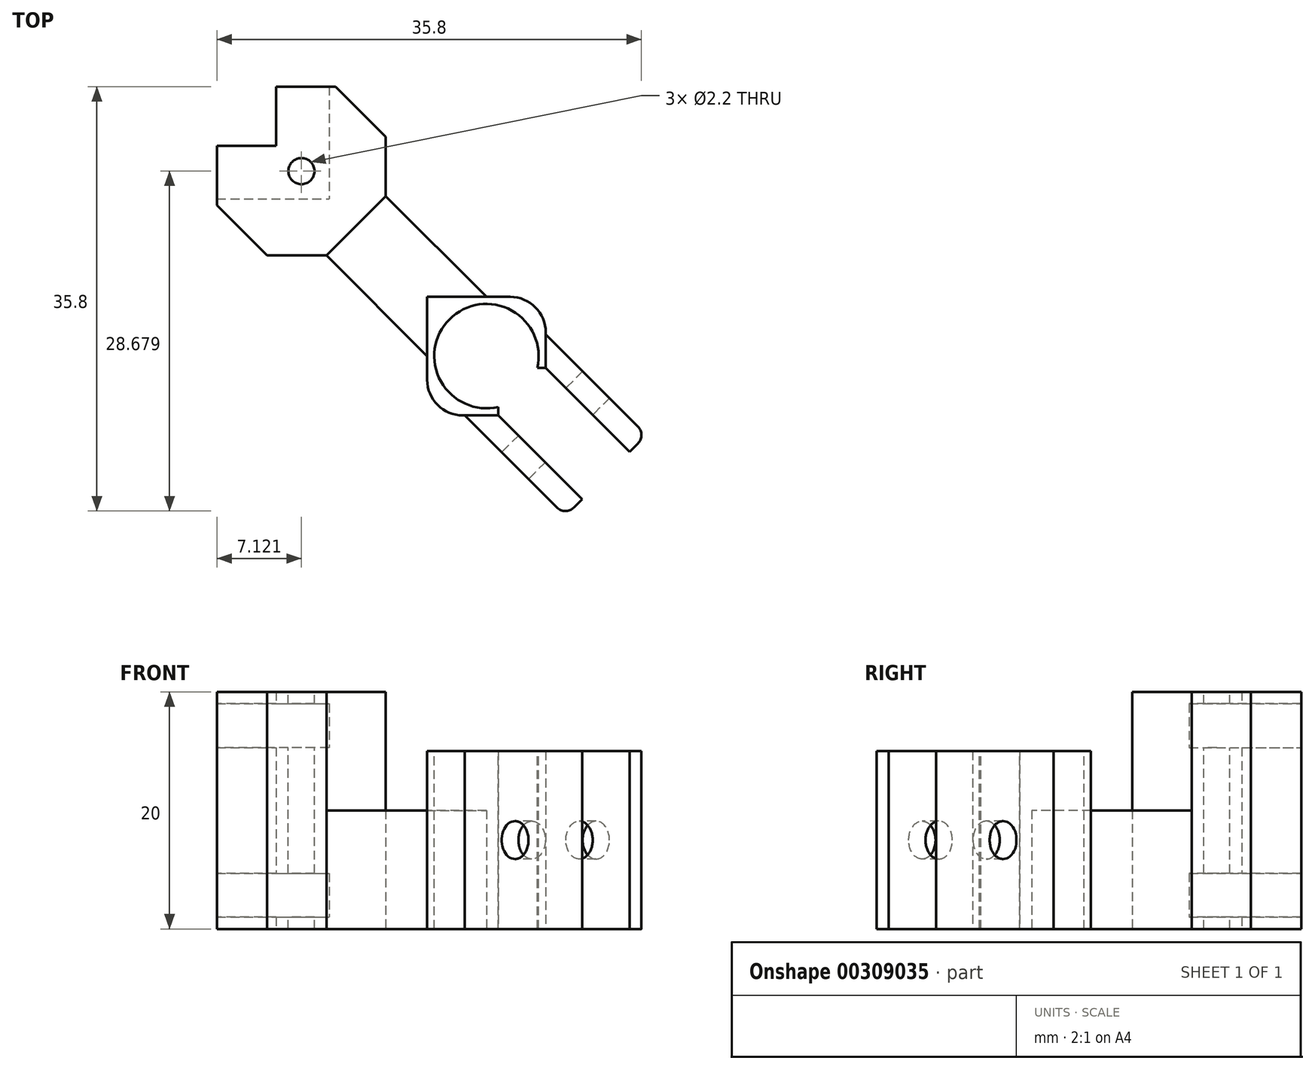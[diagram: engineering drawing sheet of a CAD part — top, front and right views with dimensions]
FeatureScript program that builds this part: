
annotation { "Feature Type Name" : "Feature", "Feature Type Description" : "" }
export const myFeature = defineFeature(function(context is Context, id is Id, definition is map)
    precondition{}
    {
        {
            var Q0;
            Q0=qCreatedBy(makeId("Top.planeOp"),FACE);
            var sketch = newSketch(context, id + "F0", { "sketchPlane" : qUnion([Q0])});
            skLineSegment(sketch, "E0", {"start": v(0, 0) * mm, "end": v(-5, 0) * mm});
            skLineSegment(sketch, "E1", {"start": v(-5, 0) * mm, "end": v(-5, 5) * mm});
            skLineSegment(sketch, "E2", {"start": v(-5, 5) * mm, "end": v(0, 5) * mm});
            skLineSegment(sketch, "E3", {"start": v(0, 5) * mm, "end": v(0, 10) * mm});
            skLineSegment(sketch, "E4", {"start": v(0, 10) * mm, "end": v(5, 10) * mm});
            skLineSegment(sketch, "E5", {"start": v(5, 10) * mm, "end": v(5, 5) * mm});
            skLineSegment(sketch, "E6", {"start": v(-5, 0) * mm, "end": v(-0.76, -4.24) * mm});
            skLineSegment(sketch, "E7", {"start": v(5, 10) * mm, "end": v(9.24, 5.76) * mm});
            skLineSegment(sketch, "E8", {"start": v(9.24, 5.76) * mm, "end": v(9.24, 0.76) * mm});
            skLineSegment(sketch, "E9", {"start": v(-0.76, -4.24) * mm, "end": v(4.24, -4.24) * mm});
            skLineSegment(sketch, "E10", {"start": v(9.24, 0.76) * mm, "end": v(17.73, -7.73) * mm});
            skLineSegment(sketch, "E11", {"start": v(4.24, -4.24) * mm, "end": v(12.73, -12.73) * mm});
            skLineSegment(sketch, "E12", {"start": v(12.73, -12.73) * mm, "end": v(12.73, -17.73) * mm});
            skLineSegment(sketch, "E13", {"start": v(12.73, -17.73) * mm, "end": v(22.73, -17.73) * mm});
            skLineSegment(sketch, "E14", {"start": v(22.73, -17.73) * mm, "end": v(22.73, -7.73) * mm});
            skLineSegment(sketch, "E15", {"start": v(22.73, -7.73) * mm, "end": v(17.73, -7.73) * mm});
            skLineSegment(sketch, "E16", {"start": v(4.24, -4.24) * mm, "end": v(9.24, 0.76) * mm});
            skPoint(sketch, "E17", {"position": v(22.73, -13.73) * mm});
            skPoint(sketch, "E18", {"position": v(18.73, -17.73) * mm});
            skLineSegment(sketch, "E19", {"start": v(22.73, -13.73) * mm, "end": v(29.8, -20.8) * mm});
            skLineSegment(sketch, "E20", {"start": v(18.73, -17.73) * mm, "end": v(25.8, -24.8) * mm});
            skLineSegment(sketch, "E21", {"start": v(29.8, -20.8) * mm, "end": v(31.21, -19.38) * mm});
            skLineSegment(sketch, "E22", {"start": v(31.21, -19.38) * mm, "end": v(22.73, -10.9) * mm});
            skLineSegment(sketch, "E23", {"start": v(25.8, -24.8) * mm, "end": v(24.38, -26.21) * mm});
            skLineSegment(sketch, "E24", {"start": v(24.38, -26.21) * mm, "end": v(15.9, -17.73) * mm});
            skSolve(sketch);
        }
        {
            var Q0;
            Q0=makeQuery(id+"F0.imprint","IMPRINT",FACE,{"disambiguationData":[TD([[makeQuery(id+"F0.imprint","IMPRINT",EDGE,{"derivedFrom":sQuery(id+"F0.wireOp",EDGE,"E1")}),-1.0]])]});
            extrude(context, id + "F1", {"entities" : qUnion([Q0]), "depth" : 20 * mm});
        }
        {
            var Q0;
            Q0=makeQuery(id+"F0.imprint","IMPRINT",FACE,{"disambiguationData":[TD([[makeQuery(id+"F0.imprint","IMPRINT",EDGE,{"derivedFrom":sQuery(id+"F0.wireOp",EDGE,"E10")}),-1.0]])]});
            extrude(context, id + "F2", {"entities" : qUnion([Q0]), "operationType" : NewBodyOperationType.ADD, "depth" : 10 * mm});
        }
        {
            var Q0;
            Q0=makeQuery(id+"F1.opExtrude","SWEPT_FACE",FACE,{"disambiguationData":[OSD([sQuery(id+"F0.wireOp",EDGE,"E4")])]});
            var sketch = newSketch(context, id + "F3", { "sketchPlane" : qUnion([Q0])});
            skPoint(sketch, "E25", {"position": v(0, 19) * mm});
            skPoint(sketch, "E26", {"position": v(0, 15.6) * mm});
            skPoint(sketch, "E27", {"position": v(0, 1) * mm});
            skPoint(sketch, "E28", {"position": v(0, 4.4) * mm});
            skLineSegment(sketch, "E29", {"start": v(0, 19) * mm, "end": v(-5, 19) * mm});
            skLineSegment(sketch, "E30", {"start": v(-5, 19) * mm, "end": v(-5, 15.6) * mm});
            skLineSegment(sketch, "E31", {"start": v(-5, 15.6) * mm, "end": v(0, 15.6) * mm});
            skSolve(sketch);
        }
        {
            var Q0;
            Q0=qSketchRegion(id+"F3",true);
            var Q1;
            {var subQ0=sQuery(id+"F3.wireOp",EDGE,"E29");Q1=makeQuery(id+"F3.imprint","IMPRINT",FACE,{"disambiguationData":[TD([[makeQuery(id+"F3.imprint","IMPRINT",EDGE,{"derivedFrom":subQ0}),1.0]])]});}
            extrude(context, id + "F4", {"entities" : qUnion([Q0, Q1]), "operationType" : NewBodyOperationType.REMOVE, "oppositeDirection" : true, "depth" : 25 * mm});
        }
        {
            var Q0;
            Q0=makeQuery(id+"F1.opExtrude","SWEPT_FACE",FACE,{"disambiguationData":[OSD([sQuery(id+"F0.wireOp",EDGE,"E2")])]});
            var sketch = newSketch(context, id + "F5", { "sketchPlane" : qUnion([Q0])});
            skLineSegment(sketch, "E32", {"start": v(0, 19) * mm, "end": v(5, 19) * mm});
            skLineSegment(sketch, "E33", {"start": v(5, 19) * mm, "end": v(5, 15.6) * mm});
            skLineSegment(sketch, "E34", {"start": v(5, 15.6) * mm, "end": v(0, 15.6) * mm});
            skLineSegment(sketch, "E35", {"start": v(0, 15.6) * mm, "end": v(0, 19) * mm});
            skSolve(sketch);
        }
        {
            var Q0;
            Q0=makeQuery(id+"F5.imprint","IMPRINT",FACE,{"disambiguationData":[TD([[makeQuery(id+"F5.imprint","IMPRINT",EDGE,{"derivedFrom":sQuery(id+"F5.wireOp",EDGE,"E32")}),-1.0]])]});
            extrude(context, id + "F6", {"entities" : qUnion([Q0]), "operationType" : NewBodyOperationType.REMOVE, "oppositeDirection" : true, "depth" : 25 * mm});
        }
        {
            var Q0;
            Q0=makeQuery(id+"F1.opExtrude","SWEPT_FACE",FACE,{"disambiguationData":[OSD([sQuery(id+"F0.wireOp",EDGE,"E7")])]});
            var sketch = newSketch(context, id + "F7", { "sketchPlane" : qUnion([Q0])});
            skLineSegment(sketch, "E36", {"start": v(3.54, 15.6) * mm, "end": v(-2.46, 15.6) * mm});
            skLineSegment(sketch, "E37", {"start": v(-2.46, 15.6) * mm, "end": v(-2.46, 19) * mm});
            skLineSegment(sketch, "E38", {"start": v(-2.46, 19) * mm, "end": v(3.54, 19) * mm});
            skLineSegment(sketch, "E39", {"start": v(3.54, 19) * mm, "end": v(3.54, 15.6) * mm});
            skSolve(sketch);
        }
        {
            var Q0;
            Q0=qSketchRegion(id+"F7",true);
            extrude(context, id + "F8", {"entities" : qUnion([Q0]), "operationType" : NewBodyOperationType.REMOVE, "oppositeDirection" : true, "depth" : 25 * mm});
        }
        {
            var Q0;
            {var subQ3=sQuery(id+"F0.wireOp",EDGE,"E4");Q0=makeQuery(id+"F4.boolean.opBoolean","SPLIT",FACE,{"disambiguationData":[TD([makeQuery(id+"F4.opExtrude","SWEPT_FACE",FACE,{"disambiguationData":[OSD([sQuery(id+"F3.wireOp",EDGE,"E31")])]})])],"derivedFrom":makeQuery(id+"F1.opExtrude","SWEPT_FACE",FACE,{"disambiguationData":[OSD([subQ3])]})});}
            var sketch = newSketch(context, id + "F9", { "sketchPlane" : qUnion([Q0])});
            skPoint(sketch, "E40", {"position": v(0, 1) * mm});
            skPoint(sketch, "E41", {"position": v(0, 4.4) * mm});
            skLineSegment(sketch, "E42.bottom", {"start": v(0, 4.4) * mm, "end": v(-5, 4.4) * mm});
            skLineSegment(sketch, "E42.top", {"start": v(0, 1) * mm, "end": v(-5, 1) * mm});
            skLineSegment(sketch, "E42.left", {"start": v(0, 4.4) * mm, "end": v(0, 1) * mm});
            skLineSegment(sketch, "E42.right", {"start": v(-5, 4.4) * mm, "end": v(-5, 1) * mm});
            skSolve(sketch);
        }
        {
            var Q0;
            Q0=qSketchRegion(id+"F9",true);
            extrude(context, id + "F10", {"entities" : qUnion([Q0]), "operationType" : NewBodyOperationType.REMOVE, "oppositeDirection" : true, "depth" : 25 * mm});
        }
        {
            var Q0;
            {var subQ3=sQuery(id+"F0.wireOp",EDGE,"E7");Q0=makeQuery(id+"F8.boolean.opBoolean","SPLIT",FACE,{"disambiguationData":[TD([makeQuery(id+"F4.boolean.opBoolean","COPY",FACE,{"derivedFrom":makeQuery(id+"F4.opExtrude","SWEPT_FACE",FACE,{"disambiguationData":[OSD([sQuery(id+"F3.wireOp",EDGE,"E31")])]})})])],"derivedFrom":makeQuery(id+"F1.opExtrude","SWEPT_FACE",FACE,{"disambiguationData":[OSD([subQ3])]})});}
            var sketch = newSketch(context, id + "F11", { "sketchPlane" : qUnion([Q0])});
            skLineSegment(sketch, "E43.bottom", {"start": v(3.54, 1) * mm, "end": v(-2.46, 1) * mm});
            skLineSegment(sketch, "E43.top", {"start": v(3.54, 4.4) * mm, "end": v(-2.46, 4.4) * mm});
            skLineSegment(sketch, "E43.left", {"start": v(3.54, 1) * mm, "end": v(3.54, 4.4) * mm});
            skLineSegment(sketch, "E43.right", {"start": v(-2.46, 1) * mm, "end": v(-2.46, 4.4) * mm});
            skSolve(sketch);
        }
        {
            var Q0;
            Q0=qSketchRegion(id+"F11",true);
            extrude(context, id + "F12", {"entities" : qUnion([Q0]), "operationType" : NewBodyOperationType.REMOVE, "oppositeDirection" : true, "depth" : 25 * mm});
        }
        {
            var Q0;
            {var subQ2=sQuery(id+"F0.wireOp",EDGE,"E2");Q0=makeQuery(id+"F6.boolean.opBoolean","SPLIT",FACE,{"disambiguationData":[TD([makeQuery(id+"F4.boolean.opBoolean","COPY",FACE,{"derivedFrom":makeQuery(id+"F4.opExtrude","SWEPT_FACE",FACE,{"disambiguationData":[OSD([sQuery(id+"F3.wireOp",EDGE,"E31")])]})})])],"derivedFrom":makeQuery(id+"F1.opExtrude","SWEPT_FACE",FACE,{"disambiguationData":[OSD([subQ2])]})});}
            var sketch = newSketch(context, id + "F13", { "sketchPlane" : qUnion([Q0])});
            skLineSegment(sketch, "E44.bottom", {"start": v(0, 4.4) * mm, "end": v(5, 4.4) * mm});
            skLineSegment(sketch, "E44.top", {"start": v(0, 1) * mm, "end": v(5, 1) * mm});
            skLineSegment(sketch, "E44.left", {"start": v(0, 4.4) * mm, "end": v(0, 1) * mm});
            skLineSegment(sketch, "E44.right", {"start": v(5, 4.4) * mm, "end": v(5, 1) * mm});
            skSolve(sketch);
        }
        {
            var Q0;
            Q0=qSketchRegion(id+"F13",true);
            extrude(context, id + "F14", {"entities" : qUnion([Q0]), "operationType" : NewBodyOperationType.REMOVE, "oppositeDirection" : true, "depth" : 25 * mm});
        }
        {
            var Q0;
            Q0=makeQuery(id+"F1.opExtrude","CAP_FACE",FACE,{"disambiguationData":[OSD([sQuery(id+"F0.wireOp",EDGE,"E1"),sQuery(id+"F0.wireOp",EDGE,"E2"),sQuery(id+"F0.wireOp",EDGE,"E3"),sQuery(id+"F0.wireOp",EDGE,"E4"),sQuery(id+"F0.wireOp",EDGE,"E6"),sQuery(id+"F0.wireOp",EDGE,"E7"),sQuery(id+"F0.wireOp",EDGE,"E8"),sQuery(id+"F0.wireOp",EDGE,"E9"),sQuery(id+"F0.wireOp",EDGE,"E16")])],"isStart":false});
            var sketch = newSketch(context, id + "F15", { "sketchPlane" : qUnion([Q0])});
            skLineSegment(sketch, "E45", {"start": v(0, 5) * mm, "end": v(0, 3.17) * mm});
            skLineSegment(sketch, "E46", {"start": v(0, 5) * mm, "end": v(2.05, 5) * mm});
            skLineSegment(sketch, "E47", {"start": v(0, 5) * mm, "end": v(2.12, 2.88) * mm});
            skSolve(sketch);
        }
        {
            var Q0;
            Q0=sQuery(id+"F15.wireOp",VERTEX,"E47.end");
            var Q1;
            Q1=makeQuery(id+"F1.opExtrude","SWEPT_BODY",BODY,{"disambiguationData":[OSD([sQuery(id+"F0.wireOp",EDGE,"E1"),sQuery(id+"F0.wireOp",EDGE,"E2"),sQuery(id+"F0.wireOp",EDGE,"E3"),sQuery(id+"F0.wireOp",EDGE,"E4"),sQuery(id+"F0.wireOp",EDGE,"E6"),sQuery(id+"F0.wireOp",EDGE,"E7"),sQuery(id+"F0.wireOp",EDGE,"E8"),sQuery(id+"F0.wireOp",EDGE,"E9"),sQuery(id+"F0.wireOp",EDGE,"E16")])]});
            hole(context, id + "F16", {"style" : HoleStyle.SIMPLE, "endStyle" : HoleEndStyle.THROUGH, "holeDiameter" : 2.2 * mm, "tappedDepth" : 12 * mm, "tapClearance" : 3, "locations" : qUnion([Q0]), "scope" : qUnion([Q1])});
        }
        {
            var Q0;
            Q0=makeQuery(id+"F2.opExtrude","CAP_FACE",FACE,{"disambiguationData":[OSD([sQuery(id+"F0.wireOp",EDGE,"E10"),sQuery(id+"F0.wireOp",EDGE,"E11"),sQuery(id+"F0.wireOp",EDGE,"E12"),sQuery(id+"F0.wireOp",EDGE,"E13"),sQuery(id+"F0.wireOp",EDGE,"E14"),sQuery(id+"F0.wireOp",EDGE,"E15"),sQuery(id+"F0.wireOp",EDGE,"E16")])],"isStart":false});
            var sketch = newSketch(context, id + "F17", { "sketchPlane" : qUnion([Q0])});
            skLineSegment(sketch, "E48", {"start": v(22.73, -7.73) * mm, "end": v(12.73, -17.73) * mm});
            skLineSegment(sketch, "E49", {"start": v(22.73, -17.73) * mm, "end": v(13.62, -8.62) * mm});
            skPoint(sketch, "E50", {"position": v(17.73, -12.73) * mm});
            skSolve(sketch);
        }
        {
            var Q0;
            Q0=sQuery(id+"F17.wireOp",VERTEX,"E50");
            var Q1;
            Q1=makeQuery(id+"F1.opExtrude","SWEPT_BODY",BODY,{"disambiguationData":[OSD([sQuery(id+"F0.wireOp",EDGE,"E1"),sQuery(id+"F0.wireOp",EDGE,"E2"),sQuery(id+"F0.wireOp",EDGE,"E3"),sQuery(id+"F0.wireOp",EDGE,"E4"),sQuery(id+"F0.wireOp",EDGE,"E6"),sQuery(id+"F0.wireOp",EDGE,"E7"),sQuery(id+"F0.wireOp",EDGE,"E8"),sQuery(id+"F0.wireOp",EDGE,"E9"),sQuery(id+"F0.wireOp",EDGE,"E16")])]});
            hole(context, id + "F18", {"style" : HoleStyle.SIMPLE, "endStyle" : HoleEndStyle.THROUGH, "holeDiameter" : 8.8 * mm, "tappedDepth" : 12 * mm, "tapClearance" : 3, "locations" : qUnion([Q0]), "scope" : qUnion([Q1])});
        }
        {
            var Q0;
            Q0=makeQuery(id+"F2.opExtrude","CAP_FACE",FACE,{"disambiguationData":[OSD([sQuery(id+"F0.wireOp",EDGE,"E10"),sQuery(id+"F0.wireOp",EDGE,"E11"),sQuery(id+"F0.wireOp",EDGE,"E12"),sQuery(id+"F0.wireOp",EDGE,"E13"),sQuery(id+"F0.wireOp",EDGE,"E14"),sQuery(id+"F0.wireOp",EDGE,"E15"),sQuery(id+"F0.wireOp",EDGE,"E16")])],"isStart":false});
            var sketch = newSketch(context, id + "F19", { "sketchPlane" : qUnion([Q0])});
            skLineSegment(sketch, "E51.bottom", {"start": v(22.73, -7.73) * mm, "end": v(12.73, -7.73) * mm});
            skLineSegment(sketch, "E51.top", {"start": v(22.73, -17.73) * mm, "end": v(12.73, -17.73) * mm});
            skLineSegment(sketch, "E51.left", {"start": v(22.73, -7.73) * mm, "end": v(22.73, -17.73) * mm});
            skLineSegment(sketch, "E51.right", {"start": v(12.73, -7.73) * mm, "end": v(12.73, -17.73) * mm});
            skSolve(sketch);
        }
        {
            var Q0;
            {var subQ1=sQuery(id+"F19.wireOp",EDGE,"E51.top");Q0=makeQuery(id+"F19.imprint","IMPRINT",FACE,{"disambiguationData":[TD([[makeQuery(id+"F19.imprint","IMPRINT",EDGE,{"derivedFrom":subQ1}),1.0]])]});}
            extrude(context, id + "F20", {"entities" : qUnion([Q0]), "operationType" : NewBodyOperationType.ADD, "depth" : 5 * mm});
        }
        {
            var Q0;
            Q0=makeQuery(id+"F8.boolean.opBoolean","MERGE",FACE,{"derivedFrom":[makeQuery(id+"F6.boolean.opBoolean","MERGE",FACE,{"derivedFrom":[makeQuery(id+"F4.boolean.opBoolean","COPY",FACE,{"derivedFrom":makeQuery(id+"F4.opExtrude","SWEPT_FACE",FACE,{"disambiguationData":[OSD([sQuery(id+"F3.wireOp",EDGE,"E31")])]})}),makeQuery(id+"F6.opExtrude","SWEPT_FACE",FACE,{"disambiguationData":[OSD([sQuery(id+"F5.wireOp",EDGE,"E34")])]})]}),makeQuery(id+"F8.opExtrude","SWEPT_FACE",FACE,{"disambiguationData":[OSD([sQuery(id+"F7.wireOp",EDGE,"E36")])]})]});
            extrude(context, id + "F21", {"entities" : qUnion([Q0]), "operationType" : NewBodyOperationType.REMOVE, "oppositeDirection" : true, "depth" : 0.3 * mm});
        }
        {
            var Q0;
            Q0=makeQuery(id+"F14.boolean.opBoolean","MERGE",FACE,{"derivedFrom":[makeQuery(id+"F12.boolean.opBoolean","MERGE",FACE,{"derivedFrom":[makeQuery(id+"F10.boolean.opBoolean","COPY",FACE,{"derivedFrom":makeQuery(id+"F10.opExtrude","SWEPT_FACE",FACE,{"disambiguationData":[OSD([sQuery(id+"F9.wireOp",EDGE,"E42.bottom")])]})}),makeQuery(id+"F12.opExtrude","SWEPT_FACE",FACE,{"disambiguationData":[OSD([sQuery(id+"F11.wireOp",EDGE,"E43.top")])]})]}),makeQuery(id+"F14.opExtrude","SWEPT_FACE",FACE,{"disambiguationData":[OSD([sQuery(id+"F13.wireOp",EDGE,"E44.bottom")])]})]});
            extrude(context, id + "F22", {"entities" : qUnion([Q0]), "operationType" : NewBodyOperationType.REMOVE, "oppositeDirection" : true, "depth" : 0.3 * mm});
        }
        {
            var Q0;
            Q0=makeQuery(id+"F20.boolean.opBoolean","MERGE",FACE,{"derivedFrom":[makeQuery(id+"F2.opExtrude","SWEPT_FACE",FACE,{"disambiguationData":[OSD([sQuery(id+"F0.wireOp",EDGE,"E13")])]}),makeQuery(id+"F20.opExtrude","SWEPT_FACE",FACE,{"disambiguationData":[OSD([sQuery(id+"F19.wireOp",EDGE,"E51.top")])]})]});
            var sketch = newSketch(context, id + "F23", { "sketchPlane" : qUnion([Q0])});
            skLineSegment(sketch, "E52", {"start": v(12.79, 15) * mm, "end": v(22.73, 15) * mm});
            skPoint(sketch, "E53", {"position": v(18.73, 15) * mm});
            skLineSegment(sketch, "E54", {"start": v(18.73, 15) * mm, "end": v(18.73, 0) * mm});
            skLineSegment(sketch, "E55", {"start": v(18.73, 0) * mm, "end": v(22.73, 0) * mm});
            skLineSegment(sketch, "E56", {"start": v(22.73, 0) * mm, "end": v(22.73, 15) * mm});
            skSolve(sketch);
        }
        {
            var Q0;
            Q0=makeQuery(id+"F20.boolean.opBoolean","MERGE",FACE,{"derivedFrom":[makeQuery(id+"F2.opExtrude","SWEPT_FACE",FACE,{"disambiguationData":[OSD([sQuery(id+"F0.wireOp",EDGE,"E14")])]}),makeQuery(id+"F20.opExtrude","SWEPT_FACE",FACE,{"disambiguationData":[OSD([sQuery(id+"F19.wireOp",EDGE,"E51.left")])]})]});
            var sketch = newSketch(context, id + "F24", { "sketchPlane" : qUnion([Q0])});
            skLineSegment(sketch, "E57", {"start": v(-17.73, 15) * mm, "end": v(-7.73, 15) * mm});
            skPoint(sketch, "E58", {"position": v(-13.73, 15) * mm});
            skLineSegment(sketch, "E59", {"start": v(-13.73, 15) * mm, "end": v(-13.73, 0) * mm});
            skLineSegment(sketch, "E60", {"start": v(-13.73, 0) * mm, "end": v(-17.73, 0) * mm});
            skLineSegment(sketch, "E61", {"start": v(-17.73, 0) * mm, "end": v(-17.73, 15) * mm});
            skSolve(sketch);
        }
        {
            var Q0;
            Q0 = qSketchRegion(id + "F24", true);
            extrude(context, id + "F25", {"entities" : qUnion([Q0]), "operationType" : NewBodyOperationType.REMOVE, "oppositeDirection" : true, "depth" : 2.4 * mm});
        }
        {
            var Q0;
            Q0 = qSketchRegion(id + "F23", true);
            extrude(context, id + "F26", {"entities" : qUnion([Q0]), "operationType" : NewBodyOperationType.REMOVE, "oppositeDirection" : true, "depth" : 3.85 * mm});
        }
        {
            var Q0;
            {var subQ0=sQuery(id+"F0.wireOp",EDGE,"E19");Q0=makeQuery(id+"F0.imprint","IMPRINT",FACE,{"disambiguationData":[TD([[makeQuery(id+"F0.imprint","IMPRINT",EDGE,{"derivedFrom":subQ0}),1.0]])]});}
            var Q1;
            {var subQ0=sQuery(id+"F0.wireOp",EDGE,"E20");Q1=makeQuery(id+"F0.imprint","IMPRINT",FACE,{"disambiguationData":[TD([[makeQuery(id+"F0.imprint","IMPRINT",EDGE,{"derivedFrom":subQ0}),-1.0]])]});}
            extrude(context, id + "F27", {"entities" : qUnion([Q0, Q1]), "depth" : 16.99 * mm});
        }
        {
            var Q0;
            Q0=makeQuery(id+"F27.opExtrude","CAP_FACE",FACE,{"disambiguationData":[OSD([sQuery(id+"F0.wireOp",EDGE,"E13"),sQuery(id+"F0.wireOp",EDGE,"E20"),sQuery(id+"F0.wireOp",EDGE,"E23"),sQuery(id+"F0.wireOp",EDGE,"E24")])],"isStart":false});
            extrude(context, id + "F28", {"entities" : qUnion([Q0]), "operationType" : NewBodyOperationType.REMOVE, "oppositeDirection" : true, "depth" : 2 * mm});
        }
        {
            var Q0;
            Q0=makeQuery(id+"F27.opExtrude","CAP_FACE",FACE,{"disambiguationData":[OSD([sQuery(id+"F0.wireOp",EDGE,"E14"),sQuery(id+"F0.wireOp",EDGE,"E19"),sQuery(id+"F0.wireOp",EDGE,"E21"),sQuery(id+"F0.wireOp",EDGE,"E22")])],"isStart":false});
            extrude(context, id + "F29", {"entities" : qUnion([Q0]), "operationType" : NewBodyOperationType.REMOVE, "oppositeDirection" : true, "depth" : 2 * mm});
        }
        {
            var Q0;
            Q0=makeQuery(id+"F27.opExtrude","SWEPT_FACE",FACE,{"disambiguationData":[OSD([sQuery(id+"F0.wireOp",EDGE,"E24")])]});
            var sketch = newSketch(context, id + "F30", { "sketchPlane" : qUnion([Q0])});
            skLineSegment(sketch, "E62", {"start": v(35.78, 15) * mm, "end": v(23.78, 0) * mm});
            skLineSegment(sketch, "E63", {"start": v(23.78, 15) * mm, "end": v(35.78, 0) * mm});
            skPoint(sketch, "E64", {"position": v(29.78, 7.5) * mm});
            skSolve(sketch);
        }
        {
            var Q0;
            Q0=sQuery(id+"F30.wireOp",VERTEX,"E64");
            var Q1;
            Q1=makeQuery(id+"F27.opExtrude","SWEPT_BODY",BODY,{"disambiguationData":[OSD([sQuery(id+"F0.wireOp",EDGE,"E13"),sQuery(id+"F0.wireOp",EDGE,"E20"),sQuery(id+"F0.wireOp",EDGE,"E23"),sQuery(id+"F0.wireOp",EDGE,"E24")])]});
            var Q2;
            Q2=makeQuery(id+"F27.opExtrude","SWEPT_BODY",BODY,{"disambiguationData":[OSD([sQuery(id+"F0.wireOp",EDGE,"E14"),sQuery(id+"F0.wireOp",EDGE,"E19"),sQuery(id+"F0.wireOp",EDGE,"E21"),sQuery(id+"F0.wireOp",EDGE,"E22")])]});
            hole(context, id + "F31", {"style" : HoleStyle.SIMPLE, "endStyle" : HoleEndStyle.THROUGH, "holeDiameter" : 3.2 * mm, "tappedDepth" : 12 * mm, "tapClearance" : 3, "locations" : qUnion([Q0]), "scope" : qUnion([Q1, Q2])});
        }
        {
            var Q0;
            Q0=makeQuery(id+"F20.boolean.opBoolean","MERGE",EDGE,{"derivedFrom":[makeQuery(id+"F2.opExtrude","SWEPT_EDGE",EDGE,{"disambiguationData":[OSD([sQuery(id+"F0.wireOp",EDGE,"E14"),sQuery(id+"F0.wireOp",EDGE,"E15")])]}),makeQuery(id+"F20.opExtrude","SWEPT_EDGE",EDGE,{"disambiguationData":[OSD([sQuery(id+"F19.wireOp",EDGE,"E51.bottom"),sQuery(id+"F19.wireOp",EDGE,"E51.left")])]})]});
            fillet(context, id + "F32", {"entities" : qUnion([Q0]), "radius" : 3 * mm, "tangentPropagation" : true, "allowEdgeOverflow" : false});
        }
        {
            var Q0;
            Q0=makeQuery(id+"F20.boolean.opBoolean","MERGE",EDGE,{"derivedFrom":[makeQuery(id+"F2.opExtrude","SWEPT_EDGE",EDGE,{"disambiguationData":[OSD([sQuery(id+"F0.wireOp",EDGE,"E12"),sQuery(id+"F0.wireOp",EDGE,"E13")])]}),makeQuery(id+"F20.opExtrude","SWEPT_EDGE",EDGE,{"disambiguationData":[OSD([sQuery(id+"F19.wireOp",EDGE,"E51.top"),sQuery(id+"F19.wireOp",EDGE,"E51.right")])]})]});
            fillet(context, id + "F33", {"entities" : qUnion([Q0]), "radius" : 3 * mm, "tangentPropagation" : true, "allowEdgeOverflow" : false});
        }
        {
            var Q0;
            Q0=makeQuery(id+"F27.opExtrude","SWEPT_EDGE",EDGE,{"disambiguationData":[OSD([sQuery(id+"F0.wireOp",EDGE,"E23"),sQuery(id+"F0.wireOp",EDGE,"E24")])]});
            fillet(context, id + "F34", {"entities" : qUnion([Q0]), "radius" : 1 * mm, "tangentPropagation" : true, "allowEdgeOverflow" : false});
        }
        {
            var Q0;
            Q0=makeQuery(id+"F27.opExtrude","SWEPT_EDGE",EDGE,{"disambiguationData":[OSD([sQuery(id+"F0.wireOp",EDGE,"E21"),sQuery(id+"F0.wireOp",EDGE,"E22")])]});
            fillet(context, id + "F35", {"entities" : qUnion([Q0]), "radius" : 1 * mm, "tangentPropagation" : true, "allowEdgeOverflow" : false});
        }
        {
            var Q0;
            Q0=makeQuery(id+"F21.boolean.opBoolean","COPY",FACE,{"derivedFrom":makeQuery(id+"F21.opExtrude","CAP_FACE",FACE,{"disambiguationData":[OSD([sQuery(id+"F3.wireOp",EDGE,"E31"),sQuery(id+"F5.wireOp",EDGE,"E34"),sQuery(id+"F7.wireOp",EDGE,"E36")])],"isStart":false})});
            var sketch = newSketch(context, id + "F36", { "sketchPlane" : qUnion([Q0])});
            skLineSegment(sketch, "E65", {"start": v(4.45, 0.55) * mm, "end": v(-5, 0.55) * mm});
            skLineSegment(sketch, "E66", {"start": v(4.45, 0.55) * mm, "end": v(4.45, 10) * mm});
            skSolve(sketch);
        }
        {
            var Q0;
            {var subQ6=sQuery(id+"F36.wireOp",EDGE,"E65");Q0=makeQuery(id+"F36.imprint","IMPRINT",FACE,{"disambiguationData":[TD([[makeQuery(id+"F36.imprint","IMPRINT",EDGE,{"derivedFrom":subQ6}),1.0]])]});}
            extrude(context, id + "F37", {"entities" : qUnion([Q0]), "operationType" : NewBodyOperationType.ADD, "depth" : 4 * mm, "hasSecondDirection" : true, "secondDirectionOppositeDirection" : true, "secondDirectionDepth" : 14.72 * mm});
        }
        {
            var Q0;
            {var subQ1=sQuery(id+"F0.wireOp",EDGE,"E9");Q0=makeQuery(id+"F37.boolean.opBoolean","SPLIT",FACE,{"disambiguationData":[TD([makeQuery(id+"F1.opExtrude","SWEPT_FACE",FACE,{"disambiguationData":[OSD([subQ1])]})])],"derivedFrom":makeQuery(id+"F14.boolean.opBoolean","MERGE",FACE,{"derivedFrom":[makeQuery(id+"F12.boolean.opBoolean","MERGE",FACE,{"derivedFrom":[makeQuery(id+"F10.boolean.opBoolean","COPY",FACE,{"derivedFrom":makeQuery(id+"F10.opExtrude","SWEPT_FACE",FACE,{"disambiguationData":[OSD([sQuery(id+"F9.wireOp",EDGE,"E42.top")])]})}),makeQuery(id+"F12.opExtrude","SWEPT_FACE",FACE,{"disambiguationData":[OSD([sQuery(id+"F11.wireOp",EDGE,"E43.bottom")])]})]}),makeQuery(id+"F14.opExtrude","SWEPT_FACE",FACE,{"disambiguationData":[OSD([sQuery(id+"F13.wireOp",EDGE,"E44.top")])]})]})});}
            extrude(context, id + "F38", {"entities" : qUnion([Q0]), "operationType" : NewBodyOperationType.ADD, "depth" : 4.73 * mm});
        }
    });
